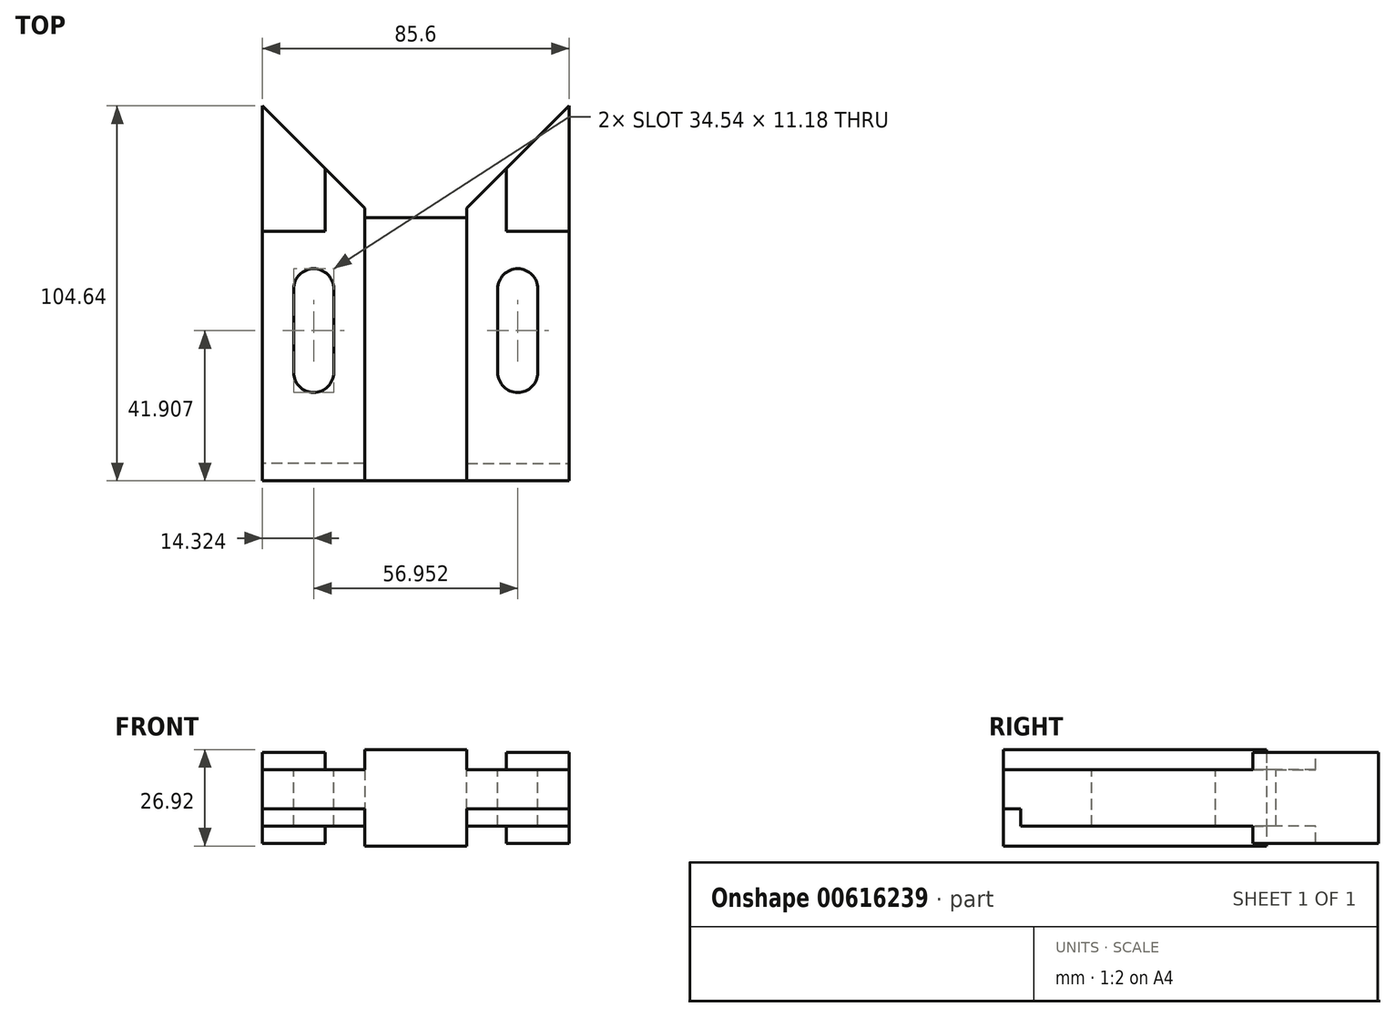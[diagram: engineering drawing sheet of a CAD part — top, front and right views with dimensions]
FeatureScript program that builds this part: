
annotation { "Feature Type Name" : "Feature", "Feature Type Description" : "" }
export const myFeature = defineFeature(function(context is Context, id is Id, definition is map)
    precondition{}
    {
        {
            var Q0;
            Q0=qCreatedBy(makeId("Top.planeOp"),FACE);
            var sketch = newSketch(context, id + "F0", { "sketchPlane" : qUnion([Q0])});
            skLineSegment(sketch, "E0.bottom", {"start": v(-14.22, 31.52) * mm, "end": v(14.22, 31.52) * mm});
            skLineSegment(sketch, "E0.top", {"start": v(-14.22, -41.88) * mm, "end": v(14.22, -41.88) * mm});
            skLineSegment(sketch, "E0.left", {"start": v(-14.22, 31.52) * mm, "end": v(-14.22, -41.88) * mm});
            skLineSegment(sketch, "E0.right", {"start": v(14.22, 31.52) * mm, "end": v(14.22, -41.88) * mm});
            skSolve(sketch);
        }
        {
            var Q0;
            Q0 = qSketchRegion(id + "F0", true);
            extrude(context, id + "F1", {"entities" : qUnion([Q0]), "depth" : 26.92 * mm, "offsetDistance" : 25.4 * mm});
        }
        {
            var Q0;
            Q0=makeQuery(id+"F1.opExtrude","SWEPT_FACE",FACE,{"disambiguationData":[OSD([sQuery(id+"F0.wireOp",EDGE,"E0.right")])]});
            var sketch = newSketch(context, id + "F2", { "sketchPlane" : qUnion([Q0])});
            skLineSegment(sketch, "E1.left", {"start": v(-41.88, 21.34) * mm, "end": v(-41.88, 5.59) * mm});
            skLineSegment(sketch, "E2", {"start": v(-41.88, 13.46) * mm, "end": v(51.95, 13.46) * mm, "construction": true});
            skPoint(sketch, "E2.startSnap0", {"position": v(-41.88, 13.46) * mm});
            skLineSegment(sketch, "E3.bottom", {"start": v(-41.88, 21.34) * mm, "end": v(62.76, 21.34) * mm, "construction": true});
            skLineSegment(sketch, "E3.top", {"start": v(-41.88, 5.59) * mm, "end": v(62.76, 5.59) * mm, "construction": true});
            skLineSegment(sketch, "E3.right", {"start": v(62.76, 21.34) * mm, "end": v(62.76, 5.59) * mm, "construction": true});
            skLineSegment(sketch, "E4.bottom", {"start": v(-41.88, 21.34) * mm, "end": v(62.76, 21.34) * mm});
            skLineSegment(sketch, "E4.top", {"start": v(-41.88, 5.59) * mm, "end": v(62.76, 5.59) * mm});
            skLineSegment(sketch, "E4.right", {"start": v(62.76, 21.34) * mm, "end": v(62.76, 5.59) * mm});
            skPoint(sketch, "E5.orphan", {"position": v(-54.83, 13.46) * mm});
            skSolve(sketch);
        }
        {
            var Q0;
            Q0 = qSketchRegion(id + "F2", true);
            extrude(context, id + "F3", {"entities" : qUnion([Q0]), "operationType" : NewBodyOperationType.ADD, "depth" : 28.57 * mm, "offsetDistance" : 25.4 * mm});
        }
        {
            var Q0;
            Q0=makeQuery(id+"F3.opExtrude","SWEPT_FACE",FACE,{"disambiguationData":[OSD([sQuery(id+"F2.wireOp",EDGE,"E4.bottom")])]});
            var sketch = newSketch(context, id + "F4", { "sketchPlane" : qUnion([Q0])});
            skLineSegment(sketch, "E6", {"start": v(0, 59.43) * mm, "end": v(0, -63.17) * mm, "construction": true});
            skLineSegment(sketch, "E7.bottom", {"start": v(14.22, 62.76) * mm, "end": v(42.8, 62.76) * mm});
            skLineSegment(sketch, "E7.top", {"start": v(14.22, -41.88) * mm, "end": v(42.8, -41.88) * mm});
            skLineSegment(sketch, "E7.left", {"start": v(14.22, 62.76) * mm, "end": v(14.22, -41.88) * mm});
            skLineSegment(sketch, "E7.right", {"start": v(42.8, 62.76) * mm, "end": v(42.8, -41.88) * mm});
            skLineSegment(sketch, "E8.MirrorCS", {"start": v(-14.22, 62.76) * mm, "end": v(-14.22, -41.88) * mm});
            skLineSegment(sketch, "E9.MirrorCS", {"start": v(-14.22, 62.76) * mm, "end": v(-42.8, 62.76) * mm});
            skLineSegment(sketch, "E10.MirrorCS", {"start": v(-42.8, 62.76) * mm, "end": v(-42.8, -41.88) * mm});
            skLineSegment(sketch, "E11.MirrorCS", {"start": v(-14.22, -41.88) * mm, "end": v(-42.8, -41.88) * mm});
            skSolve(sketch);
        }
        {
            var Q0;
            Q0 = qSketchRegion(id + "F4", true);
            extrude(context, id + "F5", {"entities" : qUnion([Q0]), "operationType" : NewBodyOperationType.ADD, "oppositeDirection" : true, "depth" : 15.75 * mm, "offsetDistance" : 25.4 * mm});
        }
        {
            var Q0;
            Q0=makeQuery(id+"F3.opExtrude","CAP_FACE",FACE,{"disambiguationData":[OSD([sQuery(id+"F2.wireOp",EDGE,"E4.bottom"),sQuery(id+"F2.wireOp",EDGE,"E4.top"),sQuery(id+"F2.wireOp",EDGE,"E4.right"),sQuery(id+"F2.wireOp",EDGE,"E1.left")])],"isStart":false});
            var sketch = newSketch(context, id + "F6", { "sketchPlane" : qUnion([Q0])});
            skLineSegment(sketch, "E12.bottom", {"start": v(-41.88, 5.59) * mm, "end": v(-37.06, 5.59) * mm});
            skLineSegment(sketch, "E12.top", {"start": v(-41.88, 10.41) * mm, "end": v(-37.06, 10.41) * mm});
            skLineSegment(sketch, "E12.left", {"start": v(-41.88, 5.59) * mm, "end": v(-41.88, 10.41) * mm});
            skLineSegment(sketch, "E12.right", {"start": v(-37.06, 5.59) * mm, "end": v(-37.06, 10.41) * mm});
            skSolve(sketch);
        }
        {
            var Q0;
            Q0 = qSketchRegion(id + "F6", true);
            var Q1;
            Q1=makeQuery(id+"F5.opExtrude","SWEPT_FACE",FACE,{"disambiguationData":[OSD([sQuery(id+"F4.wireOp",EDGE,"E10.MirrorCS")])]});
            extrude(context, id + "F7", {"entities" : qUnion([Q0, Q1]), "operationType" : NewBodyOperationType.REMOVE, "oppositeDirection" : true, "depth" : 28.57 * mm, "offsetDistance" : 25.4 * mm});
        }
        {
            var Q0;
            Q0=makeQuery(id+"F5.opExtrude","SWEPT_FACE",FACE,{"disambiguationData":[OSD([sQuery(id+"F4.wireOp",EDGE,"E10.MirrorCS")])]});
            var sketch = newSketch(context, id + "F8", { "sketchPlane" : qUnion([Q0])});
            skLineSegment(sketch, "E13.bottom", {"start": v(41.88, 5.59) * mm, "end": v(37.06, 5.59) * mm});
            skLineSegment(sketch, "E13.top", {"start": v(41.88, 10.41) * mm, "end": v(37.06, 10.41) * mm});
            skLineSegment(sketch, "E13.left", {"start": v(41.88, 5.59) * mm, "end": v(41.88, 10.41) * mm});
            skLineSegment(sketch, "E13.right", {"start": v(37.06, 5.59) * mm, "end": v(37.06, 10.41) * mm});
            skSolve(sketch);
        }
        {
            var Q0;
            Q0 = qSketchRegion(id + "F8", true);
            extrude(context, id + "F9", {"entities" : qUnion([Q0]), "operationType" : NewBodyOperationType.REMOVE, "oppositeDirection" : true, "depth" : 28.57 * mm, "offsetDistance" : 25.4 * mm});
        }
        {
            var Q0;
            Q0=makeQuery(id+"F5.opExtrude","CAP_FACE",FACE,{"disambiguationData":[OSD([sQuery(id+"F4.wireOp",EDGE,"E8.MirrorCS"),sQuery(id+"F4.wireOp",EDGE,"E9.MirrorCS"),sQuery(id+"F4.wireOp",EDGE,"E10.MirrorCS"),sQuery(id+"F4.wireOp",EDGE,"E11.MirrorCS")])],"isStart":false});
            var sketch = newSketch(context, id + "F10", { "sketchPlane" : qUnion([Q0])});
            skLineSegment(sketch, "E14.bottom", {"start": v(-42.8, 37.06) * mm, "end": v(-14.22, 37.06) * mm});
            skLineSegment(sketch, "E14.top", {"start": v(-42.8, -62.76) * mm, "end": v(-14.22, -62.76) * mm});
            skLineSegment(sketch, "E14.left", {"start": v(-42.8, 37.06) * mm, "end": v(-42.8, -62.76) * mm});
            skLineSegment(sketch, "E14.right", {"start": v(-14.22, 37.06) * mm, "end": v(-14.22, -62.76) * mm});
            skLineSegment(sketch, "E15", {"start": v(-42.8, -62.76) * mm, "end": v(-14.22, -34.19) * mm});
            skPoint(sketch, "E16.orphan", {"position": v(0, -19.97) * mm});
            skSolve(sketch);
        }
        {
            var Q0;
            {var subQ0=sQuery(id+"F10.wireOp",EDGE,"E14.top");Q0=makeQuery(id+"F10.imprint","IMPRINT",FACE,{"disambiguationData":[TD([[makeQuery(id+"F10.imprint","IMPRINT",EDGE,{"derivedFrom":subQ0}),-1.0]])]});}
            extrude(context, id + "F11", {"entities" : qUnion([Q0]), "operationType" : NewBodyOperationType.REMOVE, "oppositeDirection" : true, "depth" : 25.4 * mm, "offsetDistance" : 25.4 * mm});
        }
        {
            var Q0;
            Q0=makeQuery(id+"F3.opExtrude","SWEPT_FACE",FACE,{"disambiguationData":[OSD([sQuery(id+"F2.wireOp",EDGE,"E4.bottom")])]});
            var sketch = newSketch(context, id + "F12", { "sketchPlane" : qUnion([Q0])});
            skLineSegment(sketch, "E17.top", {"start": v(14.22, 62.76) * mm, "end": v(42.8, 62.76) * mm});
            skLineSegment(sketch, "E17.left", {"start": v(14.22, 34.19) * mm, "end": v(14.22, 62.76) * mm});
            skLineSegment(sketch, "E18", {"start": v(42.8, 62.76) * mm, "end": v(14.22, 34.19) * mm});
            skSolve(sketch);
        }
        {
            var Q0;
            Q0 = qSketchRegion(id + "F12", true);
            extrude(context, id + "F13", {"entities" : qUnion([Q0]), "operationType" : NewBodyOperationType.REMOVE, "oppositeDirection" : true, "depth" : 25.4 * mm, "offsetDistance" : 25.4 * mm});
        }
        {
            var Q0;
            Q0=makeQuery(id+"F5.opExtrude","SWEPT_FACE",FACE,{"disambiguationData":[OSD([sQuery(id+"F4.wireOp",EDGE,"E10.MirrorCS")])]});
            var sketch = newSketch(context, id + "F14", { "sketchPlane" : qUnion([Q0])});
            skLineSegment(sketch, "E19.left", {"start": v(-62.76, 21.34) * mm, "end": v(-62.76, 5.59) * mm});
            skLineSegment(sketch, "E20", {"start": v(-27.71, 21.34) * mm, "end": v(-27.71, 5.59) * mm});
            skLineSegment(sketch, "E21.bottom", {"start": v(-27.71, 26.16) * mm, "end": v(-62.76, 26.16) * mm});
            skLineSegment(sketch, "E21.top", {"start": v(-27.71, 0.76) * mm, "end": v(-62.76, 0.76) * mm});
            skLineSegment(sketch, "E21.left", {"start": v(-27.71, 26.16) * mm, "end": v(-27.71, 21.34) * mm});
            skLineSegment(sketch, "E21.right", {"start": v(-62.76, 26.16) * mm, "end": v(-62.76, 21.34) * mm});
            skLineSegment(sketch, "E22", {"start": v(61.16, 13.46) * mm, "end": v(-119.87, 13.46) * mm, "construction": true});
            skPoint(sketch, "E22.startSnap0", {"position": v(41.88, 13.46) * mm});
            skLineSegment(sketch, "E23.trimOffspring", {"start": v(-27.71, 5.59) * mm, "end": v(-27.71, 0.76) * mm});
            skLineSegment(sketch, "E24.trimOffspring", {"start": v(-62.76, 5.59) * mm, "end": v(-62.76, 0.76) * mm});
            skPoint(sketch, "E25.orphan", {"position": v(41.88, 5.59) * mm});
            skPoint(sketch, "E19.right.start.orphan", {"position": v(41.88, 21.34) * mm});
            skSolve(sketch);
        }
        {
            var Q0;
            Q0 = qSketchRegion(id + "F14", true);
            extrude(context, id + "F15", {"entities" : qUnion([Q0]), "operationType" : NewBodyOperationType.ADD, "oppositeDirection" : true, "depth" : 17.53 * mm, "offsetDistance" : 25.4 * mm});
        }
        {
            var Q0;
            Q0=makeQuery(id+"F15.opExtrude","SWEPT_FACE",FACE,{"disambiguationData":[OSD([sQuery(id+"F14.wireOp",EDGE,"E21.bottom")])]});
            var sketch = newSketch(context, id + "F16", { "sketchPlane" : qUnion([Q0])});
            skLineSegment(sketch, "E26.bottom", {"start": v(-25.27, 62.76) * mm, "end": v(-42.8, 62.76) * mm});
            skLineSegment(sketch, "E26.left", {"start": v(-25.27, 62.76) * mm, "end": v(-25.27, 45.24) * mm});
            skLineSegment(sketch, "E27", {"start": v(-42.8, 62.76) * mm, "end": v(-25.27, 45.24) * mm});
            skSolve(sketch);
        }
        {
            var Q0;
            Q0 = qSketchRegion(id + "F16", true);
            extrude(context, id + "F17", {"entities" : qUnion([Q0]), "operationType" : NewBodyOperationType.REMOVE, "oppositeDirection" : true, "depth" : 25.4 * mm, "offsetDistance" : 25.4 * mm});
        }
        {
            var Q0;
            Q0=makeQuery(id+"F3.opExtrude","CAP_FACE",FACE,{"disambiguationData":[OSD([sQuery(id+"F2.wireOp",EDGE,"E4.bottom"),sQuery(id+"F2.wireOp",EDGE,"E4.top"),sQuery(id+"F2.wireOp",EDGE,"E4.right"),sQuery(id+"F2.wireOp",EDGE,"E1.left")])],"isStart":false});
            var sketch = newSketch(context, id + "F18", { "sketchPlane" : qUnion([Q0])});
            skLineSegment(sketch, "E28.bottom", {"start": v(27.71, 21.34) * mm, "end": v(62.76, 21.34) * mm});
            skLineSegment(sketch, "E28.top", {"start": v(27.71, 5.59) * mm, "end": v(62.76, 5.59) * mm});
            skLineSegment(sketch, "E28.right", {"start": v(62.76, 21.34) * mm, "end": v(62.76, 5.59) * mm});
            skLineSegment(sketch, "E29", {"start": v(-55.98, 13.46) * mm, "end": v(111.4, 13.46) * mm, "construction": true});
            skPoint(sketch, "E29.startSnap0", {"position": v(-41.88, 13.46) * mm});
            skPoint(sketch, "E29.endSnap0", {"position": v(-41.88, 13.46) * mm});
            skPoint(sketch, "E30.oppositeSnap0", {"position": v(27.71, 13.46) * mm});
            skLineSegment(sketch, "E30.bottom", {"start": v(62.76, 26.16) * mm, "end": v(27.71, 26.16) * mm});
            skLineSegment(sketch, "E30.top", {"start": v(62.76, 0.76) * mm, "end": v(27.71, 0.76) * mm});
            skLineSegment(sketch, "E30.left", {"start": v(62.76, 26.16) * mm, "end": v(62.76, 0.76) * mm});
            skLineSegment(sketch, "E30.right", {"start": v(27.71, 26.16) * mm, "end": v(27.71, 0.76) * mm});
            skPoint(sketch, "E31.orphan", {"position": v(-41.88, 21.34) * mm});
            skPoint(sketch, "E28.left.end.orphan", {"position": v(-41.88, 5.59) * mm});
            skSolve(sketch);
        }
        {
            var Q0;
            Q0 = qSketchRegion(id + "F18", true);
            extrude(context, id + "F19", {"entities" : qUnion([Q0]), "operationType" : NewBodyOperationType.ADD, "oppositeDirection" : true, "depth" : 17.53 * mm, "offsetDistance" : 25.4 * mm});
        }
        {
            var Q0;
            Q0=makeQuery(id+"F19.opExtrude","SWEPT_FACE",FACE,{"disambiguationData":[OSD([sQuery(id+"F18.wireOp",EDGE,"E30.bottom")])]});
            var sketch = newSketch(context, id + "F20", { "sketchPlane" : qUnion([Q0])});
            skLineSegment(sketch, "E32.bottom", {"start": v(42.8, 62.76) * mm, "end": v(25.27, 62.76) * mm});
            skLineSegment(sketch, "E32.right", {"start": v(25.27, 62.76) * mm, "end": v(25.27, 45.24) * mm});
            skLineSegment(sketch, "E33", {"start": v(42.8, 62.76) * mm, "end": v(25.27, 45.24) * mm});
            skPoint(sketch, "E34.orphan", {"position": v(25.27, 27.71) * mm});
            skSolve(sketch);
        }
        {
            var Q0;
            Q0 = qSketchRegion(id + "F20", true);
            extrude(context, id + "F21", {"entities" : qUnion([Q0]), "operationType" : NewBodyOperationType.REMOVE, "oppositeDirection" : true, "depth" : 25.4 * mm, "offsetDistance" : 25.4 * mm});
        }
        {
            var Q0;
            Q0=makeQuery(id+"F5.opExtrude","CAP_FACE",FACE,{"disambiguationData":[OSD([sQuery(id+"F4.wireOp",EDGE,"E8.MirrorCS"),sQuery(id+"F4.wireOp",EDGE,"E9.MirrorCS"),sQuery(id+"F4.wireOp",EDGE,"E10.MirrorCS"),sQuery(id+"F4.wireOp",EDGE,"E11.MirrorCS")])],"isStart":true});
            var sketch = newSketch(context, id + "F22", { "sketchPlane" : qUnion([Q0])});
            skLineSegment(sketch, "E35", {"start": v(-52.81, -41.88) * mm, "end": v(58.57, -41.88) * mm, "construction": true});
            skLineSegment(sketch, "E36", {"start": v(0, 37.56) * mm, "end": v(0, -59.72) * mm, "construction": true});
            skLineSegment(sketch, "E37.left", {"start": v(-34.06, 11.71) * mm, "end": v(-34.06, -11.66) * mm});
            skLineSegment(sketch, "E37.right", {"start": v(-22.89, 11.71) * mm, "end": v(-22.89, -11.66) * mm});
            skArc(sketch, "E38", {"start": v(-34.06, 11.71) * mm, "mid": v(-28.48, 17.3) * mm, "end": v(-22.89, 11.71) * mm});
            skArc(sketch, "E39", {"start": v(-34.06, -11.66) * mm, "mid": v(-28.48, -17.25) * mm, "end": v(-22.89, -11.66) * mm});
            skArc(sketch, "E40.MirrorCS", {"start": v(34.06, 11.71) * mm, "mid": v(28.48, 17.3) * mm, "end": v(22.89, 11.71) * mm});
            skLineSegment(sketch, "E41.MirrorCS", {"start": v(34.06, 11.71) * mm, "end": v(34.06, -11.66) * mm});
            skLineSegment(sketch, "E42.MirrorCS", {"start": v(22.89, 11.71) * mm, "end": v(22.89, -11.66) * mm});
            skArc(sketch, "E43.MirrorCS", {"start": v(34.06, -11.66) * mm, "mid": v(28.48, -17.25) * mm, "end": v(22.89, -11.66) * mm});
            skSolve(sketch);
        }
        {
            var Q0;
            Q0 = qSketchRegion(id + "F22", true);
            extrude(context, id + "F23", {"entities" : qUnion([Q0]), "operationType" : NewBodyOperationType.REMOVE, "oppositeDirection" : true, "depth" : 25.4 * mm, "offsetDistance" : 25.4 * mm});
        }
    });
